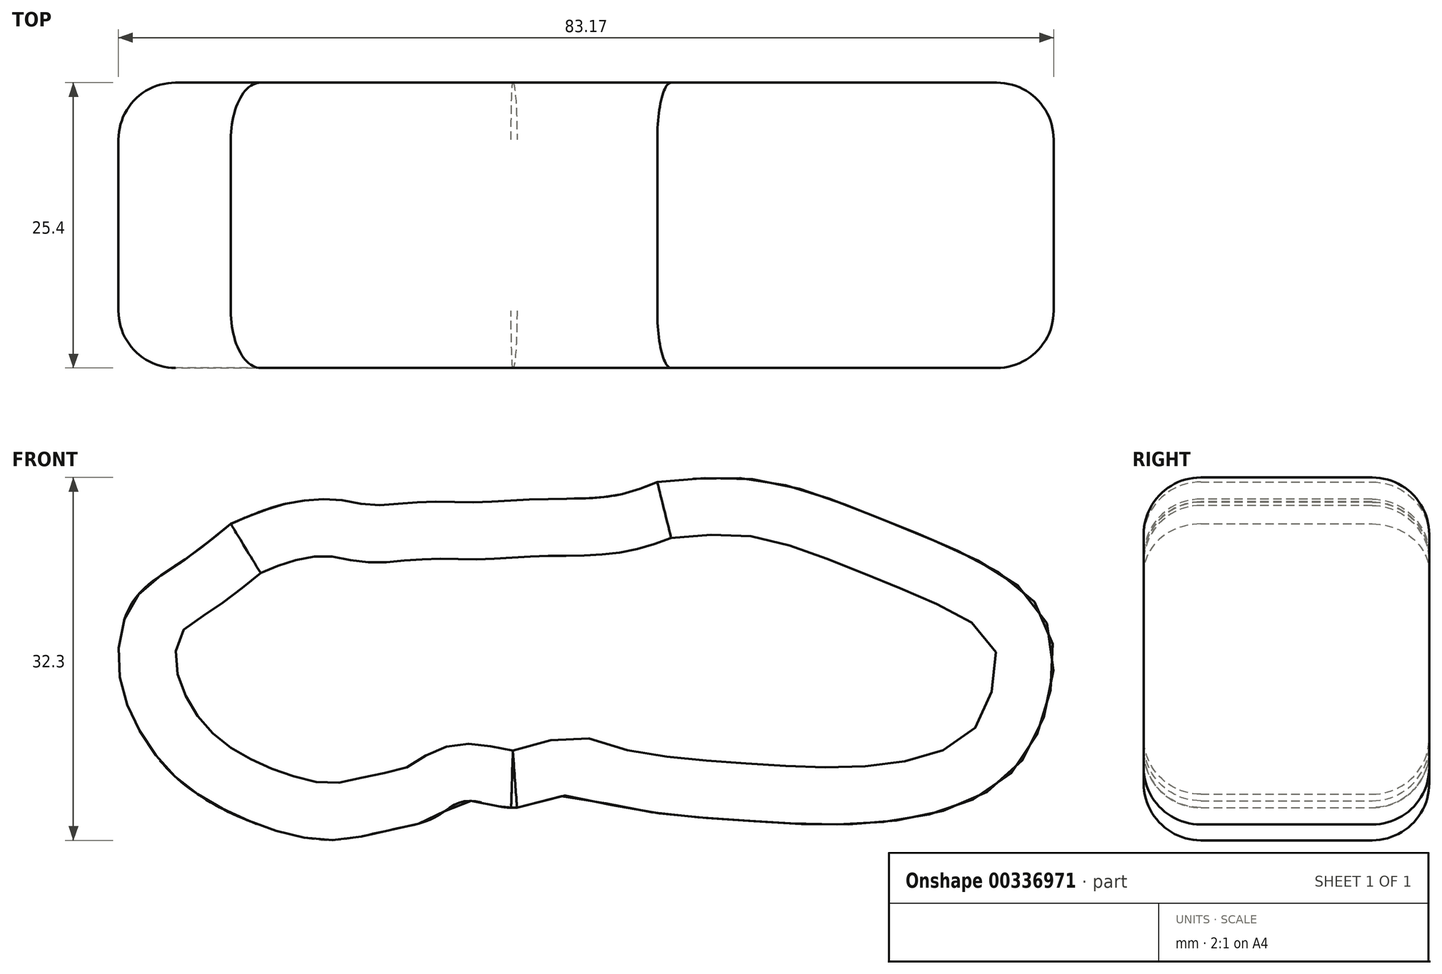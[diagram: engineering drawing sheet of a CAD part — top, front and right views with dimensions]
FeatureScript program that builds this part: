
annotation { "Feature Type Name" : "Feature", "Feature Type Description" : "" }
export const myFeature = defineFeature(function(context is Context, id is Id, definition is map)
    precondition{}
    {
        {
            var Q0;
            Q0=qCreatedBy(makeId("Front.planeOp"),FACE);
            var sketch = newSketch(context, id + "F0", { "sketchPlane" : qUnion([Q0])});
            skFitSpline(sketch, "E0", {"points": [v(-33.54, 21.11) * mm, v(-28.02, 23.04) * mm, v(-23.33, 23.18) * mm, v(-21.13, 22.77) * mm, v(-16.71, 23.04) * mm, v(-11.47, 23.04) * mm, v(-5.81, 23.32) * mm, v(0.4, 23.6) * mm, v(4.4, 24.83) * mm], "startDerivative": vector(39.01, 16.85) * mm, "endDerivative": vector(31.63, 12.72) * mm});
            skFitSpline(sketch, "E1", {"points": [v(-33.54, 21.11) * mm, v(-38.08, 17.63) * mm, v(-42.25, 14.18) * mm, v(-43.44, 7.75) * mm, v(-41.18, 1.92) * mm, v(-36.3, -3.08) * mm, v(-25.7, -7.01) * mm, v(-20.1, -6.3) * mm, v(-15.34, -4.99) * mm, v(-12.72, -3.56) * mm, v(-8.32, -4.16) * mm, v(-3.2, -2.97) * mm, v(-0.1, -3.8) * mm, v(12.75, -5.35) * mm, v(25.25, -5.35) * mm, v(35.25, -1.66) * mm, v(39.3, 5.96) * mm, v(38.1, 13.94) * mm, v(25.37, 21.11) * mm, v(13.59, 25.01) * mm, v(4.4, 24.83) * mm], "startDerivative": vector(-101.92, -83.4) * mm, "endDerivative": vector(-164.72, -17.32) * mm});
            skSolve(sketch);
        }
        {
            var Q0;
            Q0=qSketchRegion(id+"F0",true);
            extrude(context, id + "F1", {"entities" : qUnion([Q0]), "depth" : 25.4 * mm});
        }
        {
            var Q0;
            Q0=qSketchRegion(id+"F0",true);
            extrude(context, id + "F2", {"entities" : qUnion([Q0]), "operationType" : NewBodyOperationType.ADD, "depth" : 25.4 * mm});
        }
        {
            var Q0;
            Q0=makeQuery(id+"F1.opExtrude","CAP_FACE",FACE,{"disambiguationData":[OSD([sQuery(id+"F0.wireOp",EDGE,"E0"),sQuery(id+"F0.wireOp",EDGE,"E1")])],"isStart":false});
            var Q1;
            Q1=makeQuery(id+"F1.opExtrude","CAP_FACE",FACE,{"disambiguationData":[OSD([sQuery(id+"F0.wireOp",EDGE,"E0"),sQuery(id+"F0.wireOp",EDGE,"E1")])],"isStart":true});
            fillet(context, id + "F3", {"entities" : qUnion([Q0, Q1]), "radius" : 5.08 * mm, "tangentPropagation" : true, "allowEdgeOverflow" : false});
        }
    });
